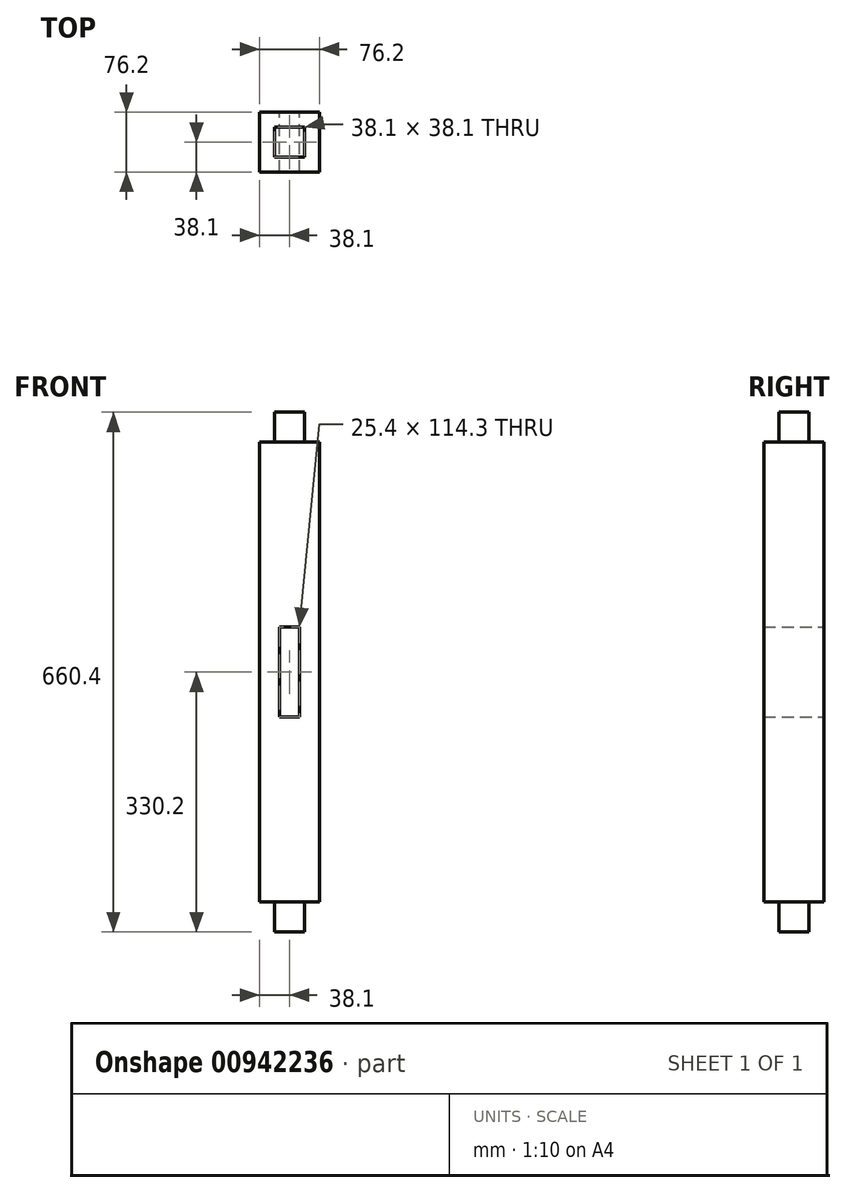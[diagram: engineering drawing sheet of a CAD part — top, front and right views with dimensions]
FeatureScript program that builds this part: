
annotation { "Feature Type Name" : "Feature", "Feature Type Description" : "" }
export const myFeature = defineFeature(function(context is Context, id is Id, definition is map)
    precondition{}
    {
        {
            var Q0;
            Q0=qCreatedBy(makeId("Top.planeOp"),FACE);
            var sketch = newSketch(context, id + "F0", { "sketchPlane" : qUnion([Q0])});
            skLineSegment(sketch, "E0.bottom", {"start": v(38.1, 38.1) * mm, "end": v(-38.1, 38.1) * mm});
            skLineSegment(sketch, "E0.top", {"start": v(38.1, -38.1) * mm, "end": v(-38.1, -38.1) * mm});
            skLineSegment(sketch, "E0.left", {"start": v(38.1, 38.1) * mm, "end": v(38.1, -38.1) * mm});
            skLineSegment(sketch, "E0.right", {"start": v(-38.1, 38.1) * mm, "end": v(-38.1, -38.1) * mm});
            skPoint(sketch, "E0.middle", {"position": v(0, 0) * mm});
            skSolve(sketch);
        }
        {
            var Q0;
            Q0 = qSketchRegion(id + "F0", true);
            extrude(context, id + "F1", {"entities" : qUnion([Q0]), "depth" : 584.2 * mm, "offsetDistance" : 25.4 * mm});
        }
        {
            var Q0;
            Q0=makeQuery(id+"F1.opExtrude","CAP_FACE",FACE,{"disambiguationData":[OSD([sQuery(id+"F0.wireOp",EDGE,"E0.bottom"),sQuery(id+"F0.wireOp",EDGE,"E0.top"),sQuery(id+"F0.wireOp",EDGE,"E0.left"),sQuery(id+"F0.wireOp",EDGE,"E0.right")])],"isStart":false});
            var sketch = newSketch(context, id + "F2", { "sketchPlane" : qUnion([Q0])});
            skLineSegment(sketch, "E1", {"start": v(38.1, -38.1) * mm, "end": v(-38.1, 38.1) * mm});
            skLineSegment(sketch, "E2.bottom", {"start": v(-19.05, 19.05) * mm, "end": v(19.05, 19.05) * mm});
            skLineSegment(sketch, "E2.top", {"start": v(-19.05, -19.05) * mm, "end": v(19.05, -19.05) * mm});
            skLineSegment(sketch, "E2.left", {"start": v(-19.05, 19.05) * mm, "end": v(-19.05, -19.05) * mm});
            skLineSegment(sketch, "E2.right", {"start": v(19.05, 19.05) * mm, "end": v(19.05, -19.05) * mm});
            skPoint(sketch, "E2.middle", {"position": v(0, 0) * mm});
            skSolve(sketch);
        }
        {
            var Q0;
            Q0 = qSketchRegion(id + "F2", true);
            extrude(context, id + "F3", {"entities" : qUnion([Q0]), "operationType" : NewBodyOperationType.ADD, "depth" : 38.1 * mm, "offsetDistance" : 25.4 * mm});
        }
        {
            var Q0;
            Q0=makeQuery(id+"F1.opExtrude","CAP_FACE",FACE,{"disambiguationData":[OSD([sQuery(id+"F0.wireOp",EDGE,"E0.bottom"),sQuery(id+"F0.wireOp",EDGE,"E0.top"),sQuery(id+"F0.wireOp",EDGE,"E0.left"),sQuery(id+"F0.wireOp",EDGE,"E0.right")])],"isStart":true});
            var sketch = newSketch(context, id + "F4", { "sketchPlane" : qUnion([Q0])});
            skLineSegment(sketch, "E3.bottom", {"start": v(19.05, -19.05) * mm, "end": v(-19.05, -19.05) * mm});
            skLineSegment(sketch, "E3.top", {"start": v(19.05, 19.05) * mm, "end": v(-19.05, 19.05) * mm});
            skLineSegment(sketch, "E3.left", {"start": v(19.05, -19.05) * mm, "end": v(19.05, 19.05) * mm});
            skLineSegment(sketch, "E3.right", {"start": v(-19.05, -19.05) * mm, "end": v(-19.05, 19.05) * mm});
            skPoint(sketch, "E3.middle", {"position": v(0, 0) * mm});
            skSolve(sketch);
        }
        {
            var Q0;
            Q0 = qSketchRegion(id + "F4", true);
            extrude(context, id + "F5", {"entities" : qUnion([Q0]), "operationType" : NewBodyOperationType.ADD, "depth" : 38.1 * mm, "offsetDistance" : 25.4 * mm});
        }
        {
            var Q0;
            Q0=makeQuery(id+"F1.opExtrude","SWEPT_FACE",FACE,{"disambiguationData":[OSD([sQuery(id+"F0.wireOp",EDGE,"E0.bottom")])]});
            var sketch = newSketch(context, id + "F6", { "sketchPlane" : qUnion([Q0])});
            skLineSegment(sketch, "E4.bottom", {"start": v(12.7, 349.25) * mm, "end": v(-12.7, 349.25) * mm});
            skLineSegment(sketch, "E4.top", {"start": v(12.7, 234.95) * mm, "end": v(-12.7, 234.95) * mm});
            skLineSegment(sketch, "E4.left", {"start": v(12.7, 349.25) * mm, "end": v(12.7, 234.95) * mm});
            skLineSegment(sketch, "E4.right", {"start": v(-12.7, 349.25) * mm, "end": v(-12.7, 234.95) * mm});
            skPoint(sketch, "E4.middle", {"position": v(0, 292.1) * mm});
            skPoint(sketch, "E5.trimOffspring.end.orphan", {"position": v(-38.1, 292.1) * mm});
            skPoint(sketch, "E6.start.orphan", {"position": v(38.1, 292.1) * mm});
            skSolve(sketch);
        }
        {
            var Q0;
            Q0 = qSketchRegion(id + "F6", true);
            extrude(context, id + "F7", {"entities" : qUnion([Q0]), "operationType" : NewBodyOperationType.REMOVE, "endBound" : BoundingType.THROUGH_ALL, "oppositeDirection" : true, "depth" : 25.4 * mm, "offsetDistance" : 25.4 * mm});
        }
    });
